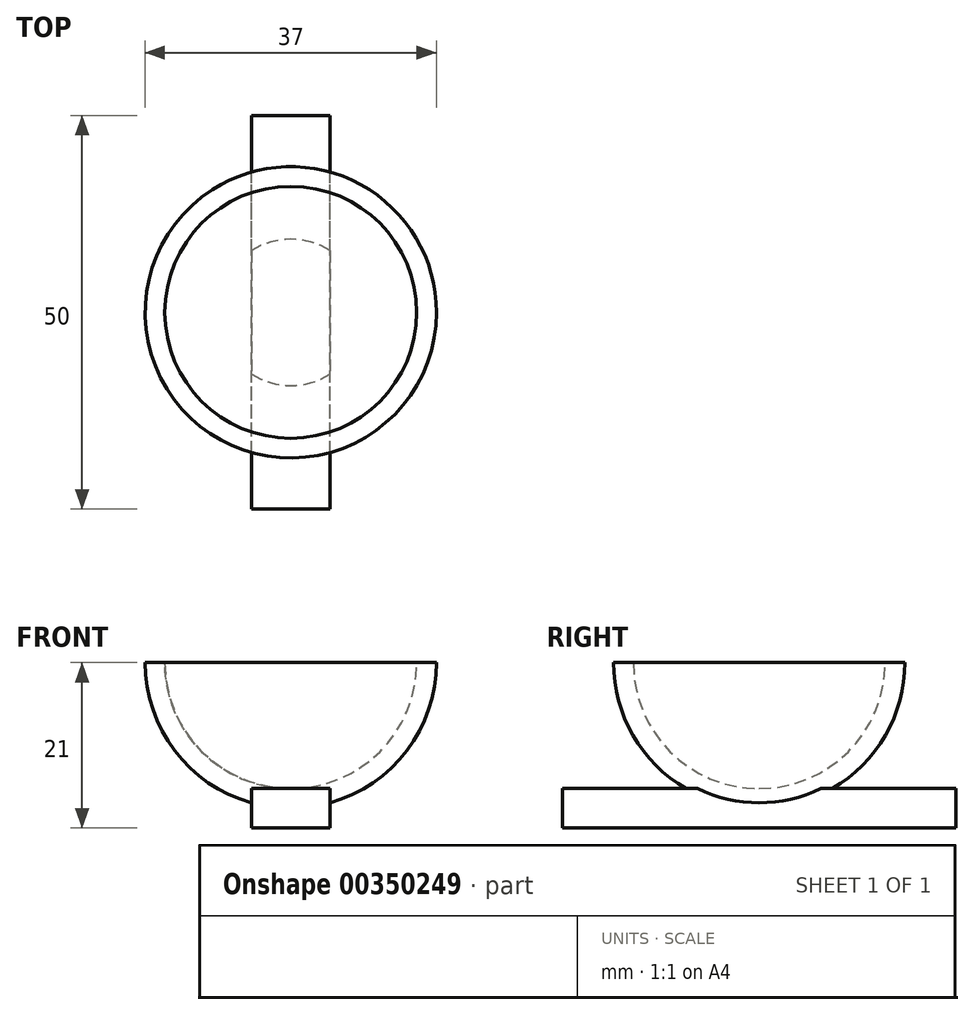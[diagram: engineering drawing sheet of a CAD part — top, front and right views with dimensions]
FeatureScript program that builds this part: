
annotation { "Feature Type Name" : "Feature", "Feature Type Description" : "" }
export const myFeature = defineFeature(function(context is Context, id is Id, definition is map)
    precondition{}
    {
        {
            var Q0;
            Q0=qCreatedBy(makeId("Front.planeOp"),FACE);
            var sketch = newSketch(context, id + "F0", { "sketchPlane" : qUnion([Q0])});
            skArc(sketch, "E0", {"start": v(-16, 0) * mm, "mid": v(-11.31, -11.31) * mm, "end": v(0, -16) * mm});
            skArc(sketch, "E1.0", {"start": v(-18.5, 0) * mm, "mid": v(-13.08, -13.08) * mm, "end": v(0, -18.5) * mm});
            skLineSegment(sketch, "E2", {"start": v(-18.5, 0) * mm, "end": v(-16, 0) * mm});
            skLineSegment(sketch, "E3", {"start": v(0, -16) * mm, "end": v(0, -18.5) * mm});
            skLineSegment(sketch, "E4.bottom", {"start": v(-5, -21) * mm, "end": v(5, -21) * mm});
            skLineSegment(sketch, "E4.top", {"start": v(-5, -16) * mm, "end": v(5, -16) * mm});
            skLineSegment(sketch, "E4.left", {"start": v(-5, -21) * mm, "end": v(-5, -16) * mm});
            skLineSegment(sketch, "E4.right", {"start": v(5, -21) * mm, "end": v(5, -16) * mm});
            skPoint(sketch, "E4.middle", {"position": v(0, -18.5) * mm});
            skLineSegment(sketch, "E5", {"start": v(0, 0) * mm, "end": v(0, -18.5) * mm, "construction": true});
            skSolve(sketch);
        }
        {
            var Q0;
            {var subQ2=sQuery(id+"F0.wireOp",EDGE,"E0");Q0=makeQuery(id+"F0.imprint","IMPRINT",FACE,{"disambiguationData":[TD([[makeQuery(id+"F0.imprint","IMPRINT",EDGE,{"derivedFrom":subQ2}),-1.0]])]});}
            var Q1;
            {var subQ0=sQuery(id+"F0.wireOp",EDGE,"E3");Q1=makeQuery(id+"F0.imprint","IMPRINT",FACE,{"disambiguationData":[TD([[makeQuery(id+"F0.imprint","IMPRINT",EDGE,{"derivedFrom":subQ0}),-1.0]])]});}
            var Q2;
            Q2=sQuery(id+"F0.wireOp",EDGE,"E5");
            revolve(context, id + "F1", {"entities" : qUnion([Q0, Q1]), "axis" : qUnion([Q2]), "revolveType" : RevolveType.FULL});
        }
        {
            var Q0;
            {var subQ1=sQuery(id+"F0.wireOp",EDGE,"E3");Q0=makeQuery(id+"F0.imprint","IMPRINT",FACE,{"disambiguationData":[TD([[makeQuery(id+"F0.imprint","IMPRINT",EDGE,{"derivedFrom":subQ1}),1.0]])]});}
            var Q1;
            {var subQ0=sQuery(id+"F0.wireOp",EDGE,"E3");Q1=makeQuery(id+"F0.imprint","IMPRINT",FACE,{"disambiguationData":[TD([[makeQuery(id+"F0.imprint","IMPRINT",EDGE,{"derivedFrom":subQ0}),-1.0]])]});}
            extrude(context, id + "F2", {"entities" : qUnion([Q0, Q1]), "operationType" : NewBodyOperationType.ADD, "endBound" : BoundingType.SYMMETRIC, "depth" : 50 * mm});
        }
    });
